# Revit family: KG111 - Continuous Hinge
name_source: partatom
category: Specialty Equipment
units: mm (PartAtom-declared; Revit-internal decimal feet)

## family parameters
Always vertical = No
Cut with Voids When Loaded = No
Part Type = Normal
Room Calculation Point = No
Round Connector Dimension = Use Diameter
Shared = No
Work Plane-Based = No

## types (1)
- KG111 - Continuous Hinge
    AssetType = Fixed
    BIMObjectName = KingswayGroup_ContinuousHinges_ContinuousHinge
    Category = Pr_30_36_36_16:Continuous hinges
    Color = For full range of available finishes and colours, contact Kingsway Group
    Default Elevation = 0 mm  [stored 0 ft]
    Description = Continuous Hinge
    DurationUnit = year
    Features = A stainless steel hinge that runs the full length of the door to provide maximum strength, security, and safety
    Finish = For full range of available finishes and colours, contact Kingsway Group
    IfcExportAs = IfcDiscreteAccessoryType
    IfcExportType = USERDEFINED
    Manufacturer = Kingsway Group
    ManufacturerName = Kingsway Group
    ManufacturerURL = https://kingswaygroupglobal.com
    Material = Stainless Steel
    Model = KG111
    ModelNumber = KG111
    ModelReference = Continuous Hinge
    Name = ContinuousHinges_ContinuousHinge_KG111_KingswayGroup
    NominalHeight = 2025 mm  [stored 6.6437 ft]
    NominalLength = 45 mm  [stored 0.147638 ft]
    NominalWidth = 9 mm  [stored 0.0295276 ft]
    PlateMaterial = NBS_Concept
    ProductInformation = https://kingswaygroupglobal.com
    Size = 45 x 2025 x 9 mm
    URL = https://kingswaygroupglobal.com
    Uniclass2015Code = Pr_30_36_36_16
    Uniclass2015Title = Continuous hinges
    Uniclass2015Version = Products v1.36
    Version = 1
    WarrantyDescription = 5-Year Guarantee *For faulty manufacture and not for damage
    WarrantyDurationParts = 5
    WarrantyDurationUnit = year

note: [stored X ft] marks values corroborated as IEEE doubles in the binary element streams (Revit-internal decimal feet)

## geometry (parser evidence)
native form markers: Sweep x2
no freeform markers — native parametric forms only
